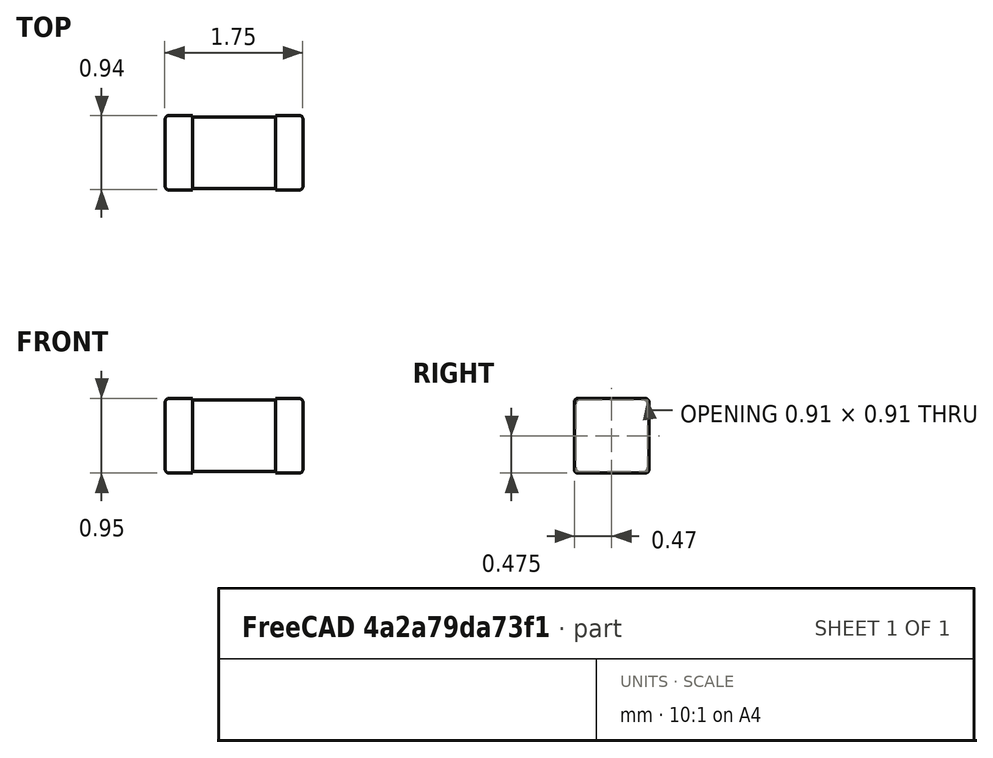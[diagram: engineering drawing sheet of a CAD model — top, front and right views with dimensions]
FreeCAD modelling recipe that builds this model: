
FCSTD DOCUMENT
Label: CAP_CHIP_1608X080
Comment: Kemet C0603... / H0.8+-0.15
objects: Part::Box×3, Part::Fillet×3, Part::MultiFuse×1
note: 7 computed .brp shape members not serialized (recipe doc carries the construction recipe); baked Part::Feature solids carry a one-line shape summary decoded from their .brp

FEATURE [Part::Box] chip
  Height = 0.91
  Length = 1.71
  Placement = pos=(-0.855,-0.455,0.02) rot=(0,0,1;0rad)
  Width = 0.91
FEATURE [Part::Fillet] chip_f
  Base = -> chip
  Edges = 4 edges r=0.05: [Edge9,Edge10,Edge11,Edge12]
FEATURE [Part::Box] plating_left
  Height = 0.95
  Length = 0.35
  Placement = pos=(-0.875,-0.475,0) rot=(0,0,1;0rad)
  Width = 0.95
FEATURE [Part::Fillet] plating_left_f
  Base = -> plating_left
  Edges = 8 edges r=0.05: [Edge1,Edge2,Edge3,Edge4,Edge9,Edge10,Edge11,Edge12]
FEATURE [Part::Box] plating_right
  Height = 0.95
  Length = 0.35
  Placement = pos=(0.525,-0.475,0) rot=(0,0,1;0rad)
  Width = 0.95
FEATURE [Part::Fillet] plating_right_f
  Base = -> plating_right
  Edges = 8 edges r=0.05: [Edge5,Edge6,Edge7,Edge8,Edge9,Edge10,Edge11,Edge12]
FEATURE [Part::MultiFuse] capacitor
  Shapes = -> [chip_f,plating_left_f,plating_right_f]
